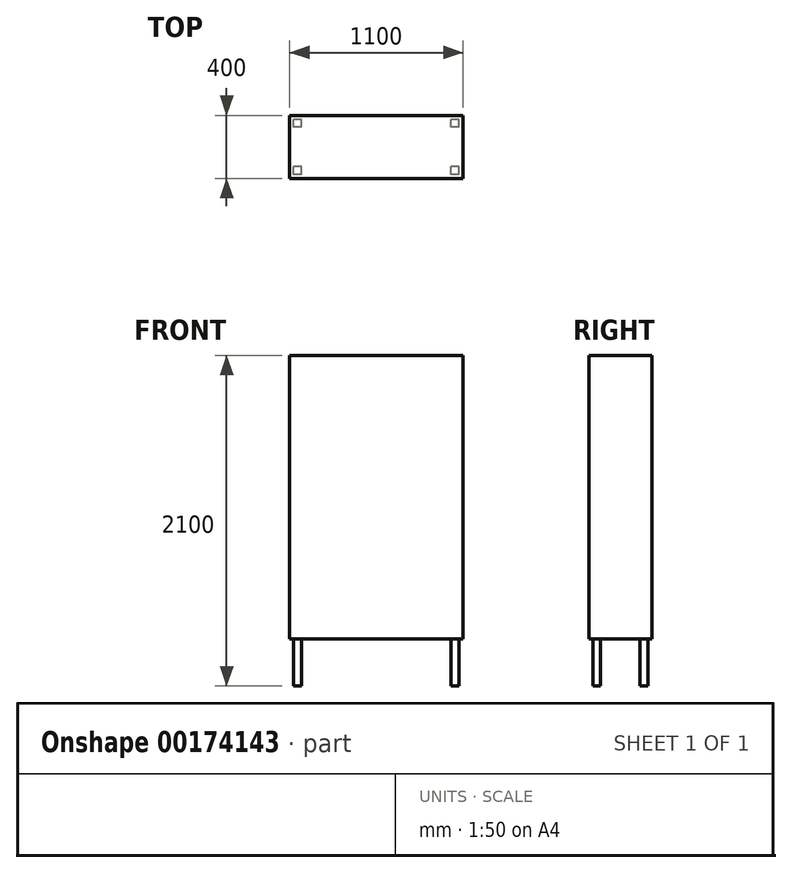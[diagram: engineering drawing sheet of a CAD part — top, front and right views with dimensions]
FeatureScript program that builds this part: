
annotation { "Feature Type Name" : "Feature", "Feature Type Description" : "" }
export const myFeature = defineFeature(function(context is Context, id is Id, definition is map)
    precondition{}
    {
        {
            var Q0;
            Q0=qCreatedBy(makeId("Top.planeOp"),FACE);
            cPlane(context, id + "F0", {"entities" : qUnion([Q0]), "cplaneType" : CPlaneType.OFFSET, "offset" : 300 * mm, "width" : 150 * mm, "height" : 150 * mm});
        }
        {
            var Q0;
            Q0=qCreatedBy(id+"F0.planeOp",FACE);
            var sketch = newSketch(context, id + "F1", { "sketchPlane" : qUnion([Q0])});
            skLineSegment(sketch, "E0.bottom", {"start": v(0, 0) * mm, "end": v(1100, 0) * mm});
            skLineSegment(sketch, "E0.top", {"start": v(0, 400) * mm, "end": v(1100, 400) * mm});
            skLineSegment(sketch, "E0.left", {"start": v(0, 0) * mm, "end": v(0, 400) * mm});
            skLineSegment(sketch, "E0.right", {"start": v(1100, 0) * mm, "end": v(1100, 400) * mm});
            skSolve(sketch);
        }
        {
            var Q0;
            Q0=makeQuery(id+"F1.imprint","IMPRINT",FACE,{"disambiguationData":[TD([[makeQuery(id+"F1.imprint","IMPRINT",EDGE,{"derivedFrom":sQuery(id+"F1.wireOp",EDGE,"E0.bottom")}),1.0]])]});
            extrude(context, id + "F2", {"entities" : qUnion([Q0]), "depth" : 1800 * mm});
        }
        {
            var Q0;
            Q0=qCreatedBy(makeId("Top.planeOp"),FACE);
            var sketch = newSketch(context, id + "F3", { "sketchPlane" : qUnion([Q0])});
            skLineSegment(sketch, "E1.bottom", {"start": v(25, 75) * mm, "end": v(75, 75) * mm});
            skLineSegment(sketch, "E1.top", {"start": v(25, 25) * mm, "end": v(75, 25) * mm});
            skLineSegment(sketch, "E1.left", {"start": v(25, 75) * mm, "end": v(25, 25) * mm});
            skLineSegment(sketch, "E1.right", {"start": v(75, 75) * mm, "end": v(75, 25) * mm});
            skLineSegment(sketch, "E2.0.1.0", {"start": v(75, 375) * mm, "end": v(75, 325) * mm});
            skLineSegment(sketch, "E2.0.1.1", {"start": v(25, 375) * mm, "end": v(25, 325) * mm});
            skLineSegment(sketch, "E2.0.1.2", {"start": v(25, 375) * mm, "end": v(75, 375) * mm});
            skLineSegment(sketch, "E2.0.1.3", {"start": v(25, 325) * mm, "end": v(75, 325) * mm});
            skLineSegment(sketch, "E2.1.0.0", {"start": v(1075, 75) * mm, "end": v(1075, 25) * mm});
            skLineSegment(sketch, "E2.1.0.1", {"start": v(1025, 75) * mm, "end": v(1025, 25) * mm});
            skLineSegment(sketch, "E2.1.0.2", {"start": v(1025, 75) * mm, "end": v(1075, 75) * mm});
            skLineSegment(sketch, "E2.1.0.3", {"start": v(1025, 25) * mm, "end": v(1075, 25) * mm});
            skLineSegment(sketch, "E2.1.1.0", {"start": v(1075, 375) * mm, "end": v(1075, 325) * mm});
            skLineSegment(sketch, "E2.1.1.1", {"start": v(1025, 375) * mm, "end": v(1025, 325) * mm});
            skLineSegment(sketch, "E2.1.1.2", {"start": v(1025, 375) * mm, "end": v(1075, 375) * mm});
            skLineSegment(sketch, "E2.1.1.3", {"start": v(1025, 325) * mm, "end": v(1075, 325) * mm});
            skLineSegment(sketch, "E2.direction1", {"start": v(25, 25) * mm, "end": v(1025, 25) * mm, "construction": true});
            skLineSegment(sketch, "E2.direction2", {"start": v(25, 25) * mm, "end": v(25, 325) * mm, "construction": true});
            skSolve(sketch);
        }
        {
            var Q0;
            Q0=makeQuery(id+"F3.imprint","IMPRINT",FACE,{"disambiguationData":[TD([[makeQuery(id+"F3.imprint","IMPRINT",EDGE,{"derivedFrom":sQuery(id+"F3.wireOp",EDGE,"E1.bottom")}),-1.0]])]});
            var Q1;
            Q1=makeQuery(id+"F3.imprint","IMPRINT",FACE,{"disambiguationData":[TD([[makeQuery(id+"F3.imprint","IMPRINT",EDGE,{"derivedFrom":sQuery(id+"F3.wireOp",EDGE,"E2.1.0.0")}),-1.0]])]});
            var Q2;
            Q2=makeQuery(id+"F3.imprint","IMPRINT",FACE,{"disambiguationData":[TD([[makeQuery(id+"F3.imprint","IMPRINT",EDGE,{"derivedFrom":sQuery(id+"F3.wireOp",EDGE,"E2.1.1.0")}),-1.0]])]});
            var Q3;
            Q3=makeQuery(id+"F3.imprint","IMPRINT",FACE,{"disambiguationData":[TD([[makeQuery(id+"F3.imprint","IMPRINT",EDGE,{"derivedFrom":sQuery(id+"F3.wireOp",EDGE,"E2.0.1.0")}),-1.0]])]});
            extrude(context, id + "F4", {"entities" : qUnion([Q0, Q1, Q2, Q3]), "operationType" : NewBodyOperationType.ADD, "depth" : 1800 * mm});
        }
    });
